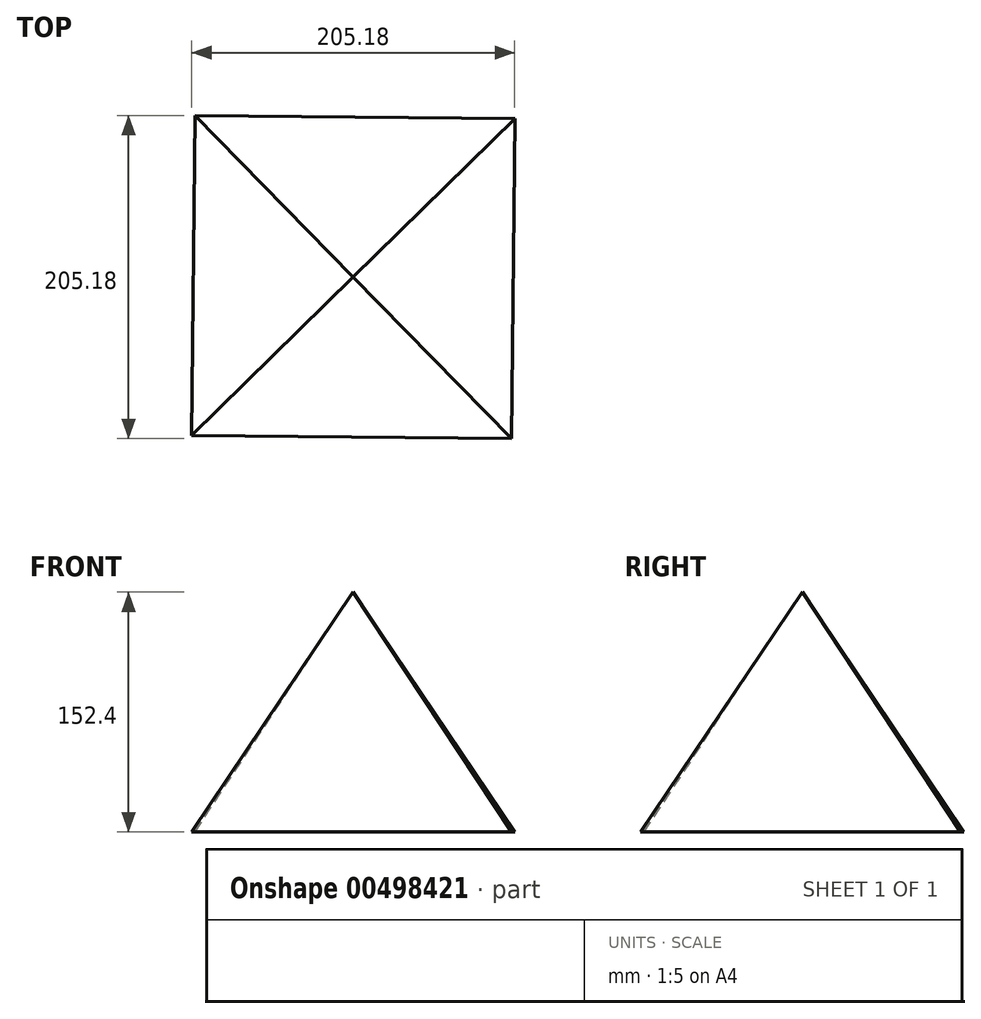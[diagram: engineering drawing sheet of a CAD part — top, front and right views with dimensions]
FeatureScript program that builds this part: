
annotation { "Feature Type Name" : "Feature", "Feature Type Description" : "" }
export const myFeature = defineFeature(function(context is Context, id is Id, definition is map)
    precondition{}
    {
        {
            var Q0;
            Q0=qCreatedBy(makeId("Top.planeOp"),FACE);
            var sketch = newSketch(context, id + "F0", { "sketchPlane" : qUnion([Q0])});
            skCircle(sketch, "E0.cCircle", {"center": v(0, 0) * mm, "radius": 143.68 * mm, "construction": true});
            skLineSegment(sketch, "E0.0", {"start": v(-100.6, 102.6) * mm, "end": v(102.6, 100.6) * mm});
            skLineSegment(sketch, "E0.1", {"start": v(102.6, 100.6) * mm, "end": v(100.6, -102.6) * mm});
            skLineSegment(sketch, "E0.2", {"start": v(100.6, -102.6) * mm, "end": v(-102.6, -100.6) * mm});
            skLineSegment(sketch, "E0.3", {"start": v(-102.6, -100.6) * mm, "end": v(-100.6, 102.6) * mm});
            skSolve(sketch);
        }
        {
            var Q0;
            Q0=qCreatedBy(makeId("Top.planeOp"),FACE);
            cPlane(context, id + "F1", {"entities" : qUnion([Q0]), "cplaneType" : CPlaneType.OFFSET, "offset" : 152.4 * mm, "width" : 152.4 * mm, "height" : 152.4 * mm});
        }
        {
            var Q0;
            Q0=qCreatedBy(id+"F1.planeOp",FACE);
            var sketch = newSketch(context, id + "F2", { "sketchPlane" : qUnion([Q0])});
            skPoint(sketch, "E1", {"position": v(0, 0) * mm});
            skSolve(sketch);
        }
        {
            var Q0;
            Q0=makeQuery(id+"F0.imprint","IMPRINT",FACE,{"disambiguationData":[TD([[makeQuery(id+"F0.imprint","IMPRINT",EDGE,{"derivedFrom":sQuery(id+"F0.wireOp",EDGE,"E0.0")}),-1.0]])]});
            var Q1;
            Q1=sQuery(id+"F2.wireOp",VERTEX,"E1");
            loft(context, id + "F3", {"sheetProfilesArray" : [{ "sheetProfileEntities" : qUnion([Q0]) }, { "sheetProfileEntities" : qUnion([Q1]) }]});
        }
    });
